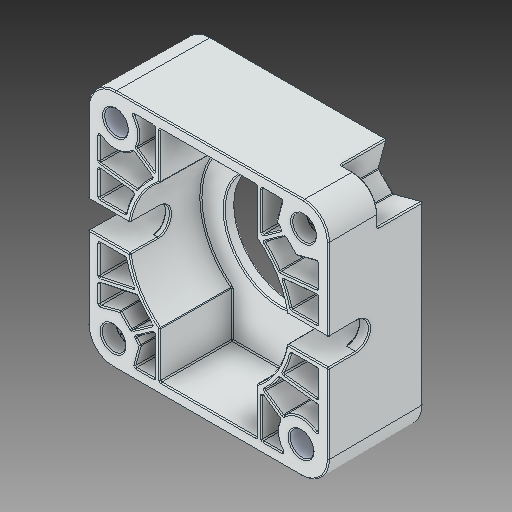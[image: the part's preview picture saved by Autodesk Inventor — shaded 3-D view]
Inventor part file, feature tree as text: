
AUTODESK INVENTOR PART (.ipt)
format: ipt  version: 2018 (Build 220112000, 112)  size: 1,379,840 bytes
history: native  units: in
note: dims shown in document units (in); Inventor stores cm internally (conversion verified against a paired STEP export)
features: fillet x1
ambient origin geometry x8: Origin, YZ Plane, XZ Plane, XY Plane, X Axis, Y Axis, Z Axis, Center Point
bodies: Solid1 (feature_tree)
feature tree (1):
  fillet  "Fillet7"  [1 undecoded]
note: 1 required parameter value undecoded (feature->parameter linkage not recoverable at this tier; creation-order binding heuristic only, values carry confidence <= 0.55)
